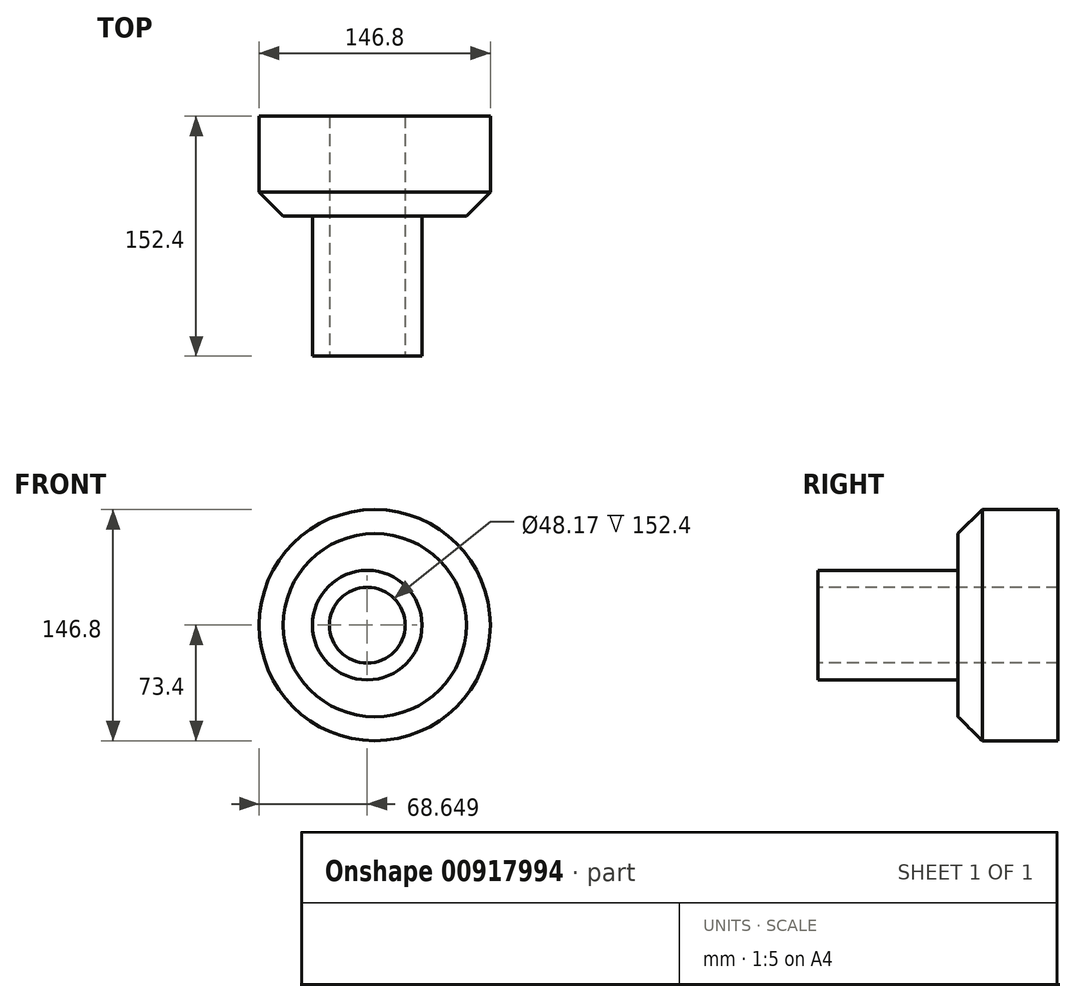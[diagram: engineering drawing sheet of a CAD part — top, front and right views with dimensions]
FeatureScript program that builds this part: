
annotation { "Feature Type Name" : "Feature", "Feature Type Description" : "" }
export const myFeature = defineFeature(function(context is Context, id is Id, definition is map)
    precondition{}
    {
        {
            var Q0;
            Q0=qCreatedBy(makeId("Front.planeOp"),FACE);
            var sketch = newSketch(context, id + "F0", { "sketchPlane" : qUnion([Q0])});
            skCircle(sketch, "E0", {"center": v(0, 0) * mm, "radius": 73.4 * mm});
            skSolve(sketch);
        }
        {
            var Q0;
            Q0=makeQuery(id+"F0.imprint","IMPRINT",FACE,{"disambiguationData":[TD([[makeQuery(id+"F0.imprint","IMPRINT",EDGE,{"derivedFrom":sQuery(id+"F0.wireOp",EDGE,"E0")}),1.0]])]});
            extrude(context, id + "F1", {"entities" : qUnion([Q0]), "depth" : 63.5 * mm, "offsetDistance" : 25.4 * mm});
        }
        {
            var Q0;
            Q0=makeQuery(id+"F1.opExtrude","CAP_EDGE",EDGE,{"disambiguationData":[OSD([sQuery(id+"F0.wireOp",EDGE,"E0")])],"isStart":false});
            chamfer(context, id + "F2", {"entities" : qUnion([Q0]), "width" : 15.24 * mm, "tangentPropagation" : true});
        }
        {
            var Q0;
            Q0=makeQuery(id+"F1.opExtrude","CAP_FACE",FACE,{"disambiguationData":[OSD([sQuery(id+"F0.wireOp",EDGE,"E0")])],"isStart":false});
            var sketch = newSketch(context, id + "F3", { "sketchPlane" : qUnion([Q0])});
            skCircle(sketch, "E1", {"center": v(-4.75, 0) * mm, "radius": 34.8 * mm});
            skSolve(sketch);
        }
        {
            var Q0;
            Q0=makeQuery(id+"F3.imprint","IMPRINT",FACE,{"disambiguationData":[TD([[makeQuery(id+"F3.imprint","IMPRINT",EDGE,{"derivedFrom":sQuery(id+"F3.wireOp",EDGE,"E1")}),1.0]])]});
            extrude(context, id + "F4", {"entities" : qUnion([Q0]), "operationType" : NewBodyOperationType.ADD, "depth" : 88.9 * mm, "offsetDistance" : 25.4 * mm});
        }
        {
            var Q0;
            Q0=makeQuery(id+"F4.opExtrude","CAP_FACE",FACE,{"disambiguationData":[OSD([sQuery(id+"F3.wireOp",EDGE,"E1")])],"isStart":false});
            var sketch = newSketch(context, id + "F5", { "sketchPlane" : qUnion([Q0])});
            skCircle(sketch, "E2", {"center": v(-4.75, 0) * mm, "radius": 24.09 * mm});
            skSolve(sketch);
        }
        {
            var Q0;
            Q0=makeQuery(id+"F5.imprint","IMPRINT",FACE,{"disambiguationData":[TD([[makeQuery(id+"F5.imprint","IMPRINT",EDGE,{"derivedFrom":sQuery(id+"F5.wireOp",EDGE,"E2")}),1.0]])]});
            extrude(context, id + "F6", {"entities" : qUnion([Q0]), "operationType" : NewBodyOperationType.REMOVE, "oppositeDirection" : true, "depth" : 263.4 * mm, "offsetDistance" : 25.4 * mm});
        }
    });
